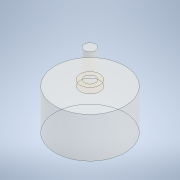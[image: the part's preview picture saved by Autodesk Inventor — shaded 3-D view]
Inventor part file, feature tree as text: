
AUTODESK INVENTOR PART (.ipt)
format: ipt  version: 2020 (Build 240168000, 168)  size: 115,712 bytes
history: native  units: mm
features: extrude x3, sketch x3, other x2
ambient origin geometry x8: Origin, YZ Plane, XZ Plane, XY Plane, X Axis, Y Axis, Z Axis, Center Point
bodies: Body1 (feature_tree), Body2 (feature_tree)
feature tree (8):
  other  "Bryła1"
  extrude  "Wyciągnięcie proste1"  Depth=25.0mm
  extrude  "Wyciągnięcie proste2"  Depth=14.5mm TaperAngle=0.0deg
  extrude  "Wyciągnięcie proste3"  Depth=7.0mm
  sketch  "Szkic1"
  sketch  "Szkic2"
  other  "Bryła2"
  sketch  "Szkic3"
